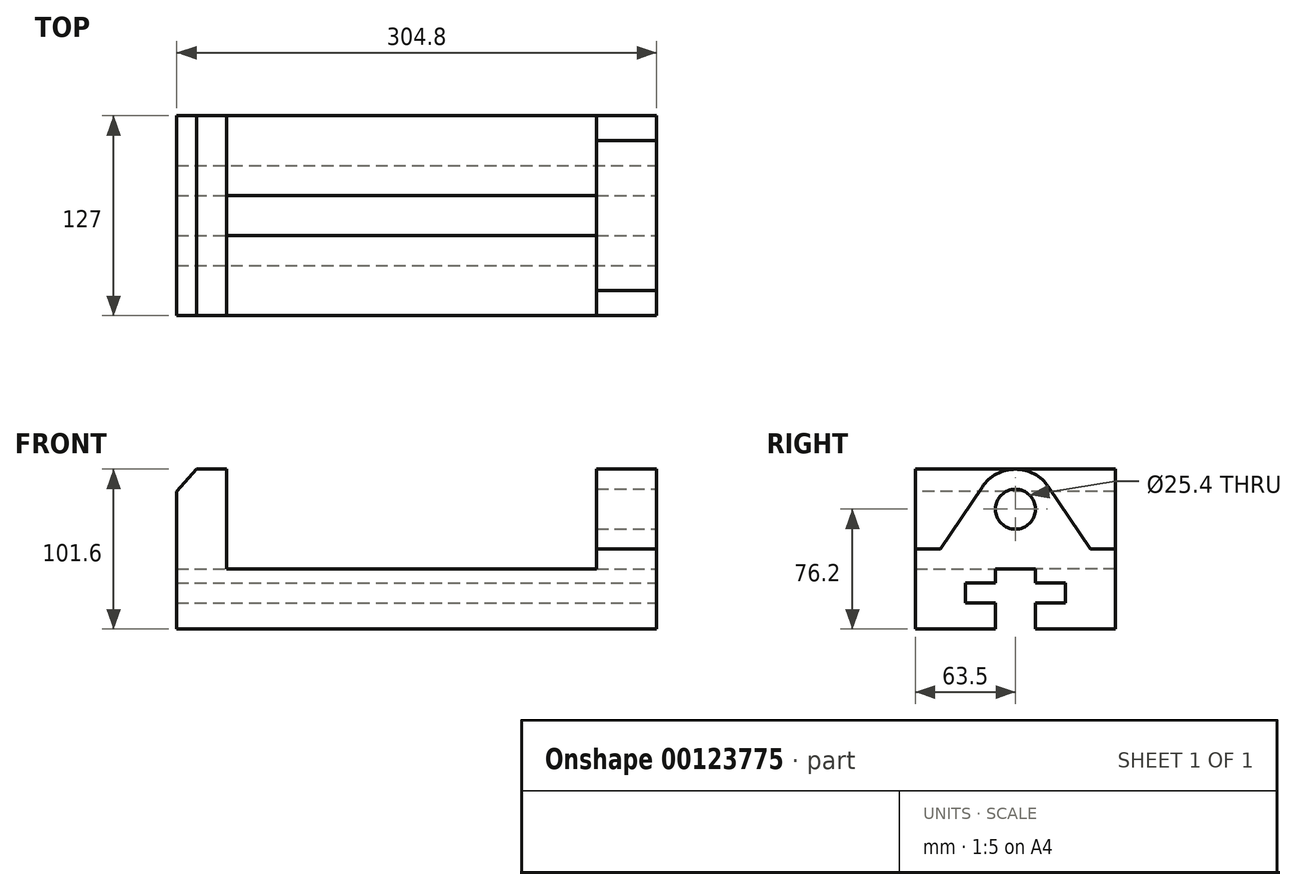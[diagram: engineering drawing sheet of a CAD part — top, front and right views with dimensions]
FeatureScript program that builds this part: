
annotation { "Feature Type Name" : "Feature", "Feature Type Description" : "" }
export const myFeature = defineFeature(function(context is Context, id is Id, definition is map)
    precondition{}
    {
        {
            var Q0;
            Q0=qCreatedBy(makeId("Right.planeOp"),FACE);
            var sketch = newSketch(context, id + "F0", { "sketchPlane" : qUnion([Q0])});
            skLineSegment(sketch, "E0", {"start": v(0, 0) * mm, "end": v(0, 50.8) * mm});
            skLineSegment(sketch, "E1", {"start": v(127, 0) * mm, "end": v(0, 0) * mm});
            skLineSegment(sketch, "E2", {"start": v(127, 0) * mm, "end": v(127, 50.8) * mm});
            skLineSegment(sketch, "E3", {"start": v(0, 50.8) * mm, "end": v(15.87, 50.8) * mm});
            skLineSegment(sketch, "E4", {"start": v(127, 50.8) * mm, "end": v(111.12, 50.8) * mm});
            skLineSegment(sketch, "E5", {"start": v(15.88, 50.8) * mm, "end": v(42.4, 90.35) * mm});
            skLineSegment(sketch, "E6", {"start": v(111.13, 50.8) * mm, "end": v(84.6, 90.35) * mm});
            skArc(sketch, "E7", {"start": v(42.4, 90.35) * mm, "mid": v(63.5, 101.6) * mm, "end": v(84.6, 90.35) * mm});
            skCircle(sketch, "E8", {"center": v(63.5, 76.2) * mm, "radius": 12.7 * mm});
            skLineSegment(sketch, "E9", {"start": v(63.5, 101.6) * mm, "end": v(-10.7, 101.6) * mm, "construction": true});
            skPoint(sketch, "E9.startSnap0", {"position": v(63.5, 101.6) * mm});
            skLineSegment(sketch, "E10", {"start": v(50.8, 0) * mm, "end": v(50.8, 16.5) * mm});
            skLineSegment(sketch, "E11", {"start": v(50.8, 16.5) * mm, "end": v(31.75, 16.5) * mm});
            skLineSegment(sketch, "E12", {"start": v(31.75, 16.5) * mm, "end": v(31.75, 29.2) * mm});
            skLineSegment(sketch, "E13", {"start": v(95.25, 29.2) * mm, "end": v(95.25, 16.51) * mm});
            skLineSegment(sketch, "E14", {"start": v(95.25, 16.5) * mm, "end": v(76.2, 16.5) * mm});
            skLineSegment(sketch, "E15", {"start": v(76.2, 16.5) * mm, "end": v(76.2, 0) * mm});
            skLineSegment(sketch, "E16", {"start": v(31.75, 29.2) * mm, "end": v(50.8, 29.2) * mm});
            skLineSegment(sketch, "E17", {"start": v(50.8, 29.2) * mm, "end": v(50.8, 38.1) * mm});
            skLineSegment(sketch, "E18", {"start": v(50.8, 38.1) * mm, "end": v(76.2, 38.1) * mm});
            skLineSegment(sketch, "E19", {"start": v(76.2, 38.1) * mm, "end": v(76.2, 29.2) * mm});
            skLineSegment(sketch, "E20", {"start": v(76.2, 29.2) * mm, "end": v(95.25, 29.2) * mm});
            skSolve(sketch);
        }
        {
            var Q0;
            Q0=qCreatedBy(makeId("Front.planeOp"),FACE);
            var sketch = newSketch(context, id + "F1", { "sketchPlane" : qUnion([Q0])});
            skLineSegment(sketch, "E21", {"start": v(0, 38.1) * mm, "end": v(-273.05, 38.1) * mm});
            skLineSegment(sketch, "E22", {"start": v(-273.05, 38.1) * mm, "end": v(-273.05, 101.6) * mm});
            skLineSegment(sketch, "E23", {"start": v(-273.05, 101.6) * mm, "end": v(-292.02, 101.6) * mm});
            skLineSegment(sketch, "E24", {"start": v(-292.02, 101.6) * mm, "end": v(-304.8, 87.47) * mm});
            skLineSegment(sketch, "E25", {"start": v(-304.8, 87.47) * mm, "end": v(-304.8, 0) * mm});
            skLineSegment(sketch, "E26", {"start": v(-304.8, 0) * mm, "end": v(0, 0) * mm});
            skLineSegment(sketch, "E27", {"start": v(0, 38.1) * mm, "end": v(0, 0) * mm});
            skSolve(sketch);
        }
        {
            var Q0;
            {var subQ1=sQuery(id+"F0.wireOp",EDGE,"E0");Q0=makeQuery(id+"F0.imprint","IMPRINT",FACE,{"disambiguationData":[TD([[makeQuery(id+"F0.imprint","IMPRINT",EDGE,{"derivedFrom":subQ1}),-1.0]])]});}
            extrude(context, id + "F2", {"entities" : qUnion([Q0]), "oppositeDirection" : true, "depth" : 38.1 * mm});
        }
        {
            var Q0;
            Q0=makeQuery(id+"F1.imprint","IMPRINT",FACE,{"disambiguationData":[TD([[makeQuery(id+"F1.imprint","IMPRINT",EDGE,{"derivedFrom":sQuery(id+"F1.wireOp",EDGE,"E21")}),1.0]])]});
            extrude(context, id + "F3", {"entities" : qUnion([Q0]), "operationType" : NewBodyOperationType.ADD, "oppositeDirection" : true, "depth" : 127 * mm});
        }
        {
            var Q0;
            {var subQ0=sQuery(id+"F0.wireOp",EDGE,"E10");Q0=makeQuery(id+"F0.imprint","IMPRINT",FACE,{"disambiguationData":[TD([[makeQuery(id+"F0.imprint","IMPRINT",EDGE,{"derivedFrom":subQ0}),-1.0]])]});}
            extrude(context, id + "F4", {"entities" : qUnion([Q0]), "operationType" : NewBodyOperationType.REMOVE, "endBound" : BoundingType.THROUGH_ALL, "oppositeDirection" : true, "depth" : 25.4 * mm});
        }
    });
